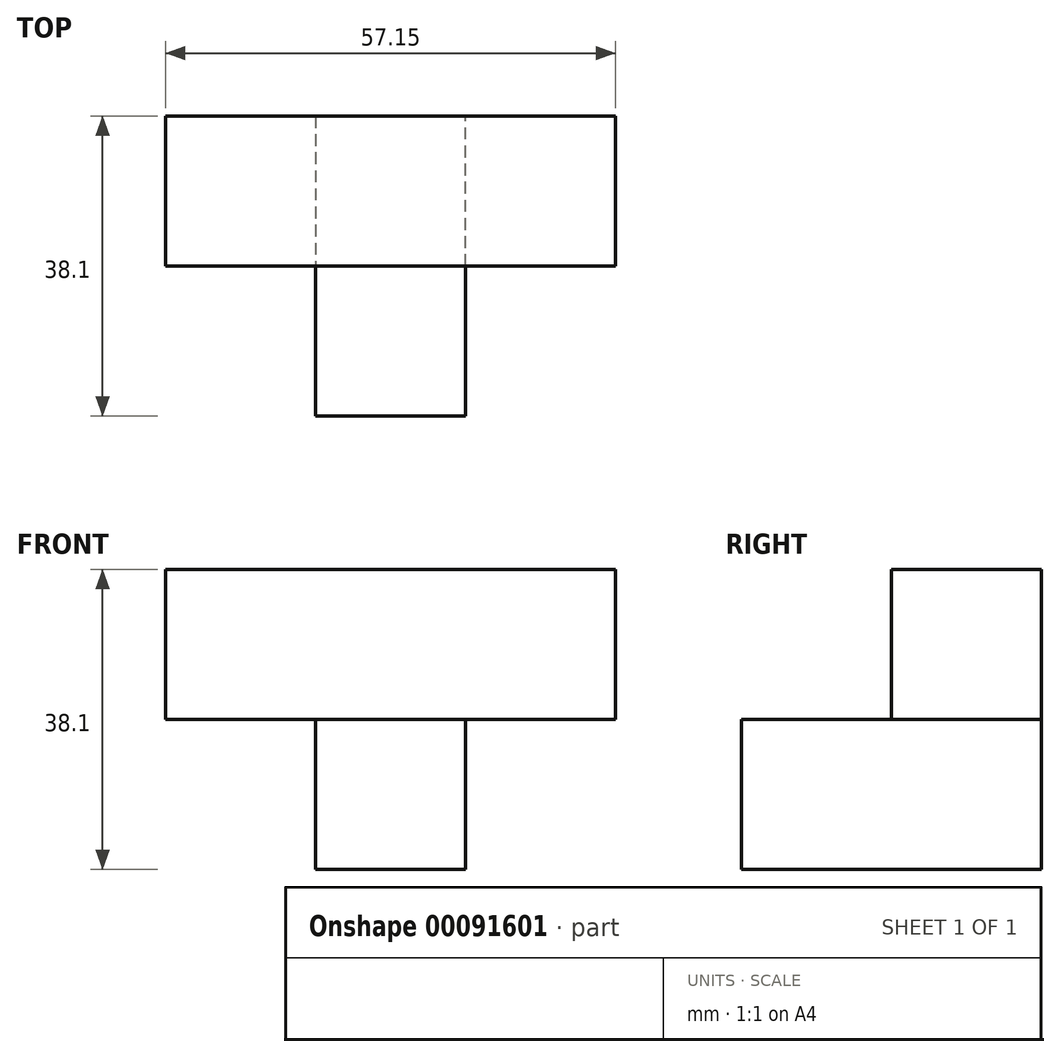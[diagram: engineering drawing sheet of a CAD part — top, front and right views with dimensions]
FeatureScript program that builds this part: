
annotation { "Feature Type Name" : "Feature", "Feature Type Description" : "" }
export const myFeature = defineFeature(function(context is Context, id is Id, definition is map)
    precondition{}
    {
        {
            var Q0;
            Q0=qCreatedBy(makeId("Top.planeOp"),FACE);
            var sketch = newSketch(context, id + "F0", { "sketchPlane" : qUnion([Q0])});
            skLineSegment(sketch, "E0.bottom", {"start": v(-19.05, 35.05) * mm, "end": v(0, 35.05) * mm});
            skLineSegment(sketch, "E0.top", {"start": v(-19.05, 16) * mm, "end": v(0, 16) * mm});
            skLineSegment(sketch, "E0.left", {"start": v(-19.05, 35.05) * mm, "end": v(-19.05, 16) * mm});
            skLineSegment(sketch, "E0.right", {"start": v(0, 35.05) * mm, "end": v(0, 16) * mm});
            skSolve(sketch);
        }
        {
            var Q0;
            Q0 = qSketchRegion(id + "F0", true);
            var Q1;
            Q1=makeQuery(id+"F0.imprint","IMPRINT",FACE,{"disambiguationData":[TD([[makeQuery(id+"F0.imprint","IMPRINT",EDGE,{"derivedFrom":sQuery(id+"F0.wireOp",EDGE,"E0.bottom")}),-1.0]])]});
            extrude(context, id + "F1", {"entities" : qUnion([Q0, Q1]), "depth" : 19.05 * mm});
        }
        {
            var Q0;
            Q0=makeQuery(id+"F1.opExtrude","CAP_FACE",FACE,{"disambiguationData":[OSD([sQuery(id+"F0.wireOp",EDGE,"E0.bottom"),sQuery(id+"F0.wireOp",EDGE,"E0.top"),sQuery(id+"F0.wireOp",EDGE,"E0.left"),sQuery(id+"F0.wireOp",EDGE,"E0.right")])],"isStart":false});
            extrude(context, id + "F2", {"entities" : qUnion([Q0]), "operationType" : NewBodyOperationType.ADD, "depth" : 19.05 * mm});
        }
        {
            var Q0;
            {var subQ0=sQuery(id+"F0.wireOp",EDGE,"E0.top");Q0=makeQuery(id+"F2.boolean.opBoolean","MERGE",FACE,{"derivedFrom":[makeQuery(id+"F1.opExtrude","SWEPT_FACE",FACE,{"disambiguationData":[OSD([subQ0])]}),makeQuery(id+"F2.opExtrude","SWEPT_FACE",FACE,{"disambiguationData":[OSD([subQ0])]})]});}
            var sketch = newSketch(context, id + "F3", { "sketchPlane" : qUnion([Q0])});
            skLineSegment(sketch, "E1.bottom", {"start": v(-19.05, 0) * mm, "end": v(0, 0) * mm});
            skLineSegment(sketch, "E1.top", {"start": v(-19.05, 19.05) * mm, "end": v(0, 19.05) * mm});
            skLineSegment(sketch, "E1.left", {"start": v(-19.05, 0) * mm, "end": v(-19.05, 19.05) * mm});
            skLineSegment(sketch, "E1.right", {"start": v(0, 0) * mm, "end": v(0, 19.05) * mm});
            skSolve(sketch);
        }
        {
            var Q0;
            Q0 = qSketchRegion(id + "F3", true);
            extrude(context, id + "F4", {"entities" : qUnion([Q0]), "operationType" : NewBodyOperationType.ADD, "depth" : 19.05 * mm});
        }
        {
            var Q0;
            {var subQ0=sQuery(id+"F0.wireOp",EDGE,"E0.right");Q0=makeQuery(id+"F4.boolean.opBoolean","MERGE",FACE,{"derivedFrom":[makeQuery(id+"F2.boolean.opBoolean","MERGE",FACE,{"derivedFrom":[makeQuery(id+"F1.opExtrude","SWEPT_FACE",FACE,{"disambiguationData":[OSD([subQ0])]}),makeQuery(id+"F2.opExtrude","SWEPT_FACE",FACE,{"disambiguationData":[OSD([subQ0])]})]}),makeQuery(id+"F4.opExtrude","SWEPT_FACE",FACE,{"disambiguationData":[OSD([sQuery(id+"F3.wireOp",EDGE,"E1.right")])]})]});}
            var sketch = newSketch(context, id + "F5", { "sketchPlane" : qUnion([Q0])});
            skLineSegment(sketch, "E2.bottom", {"start": v(16, 38.1) * mm, "end": v(35.05, 38.1) * mm});
            skLineSegment(sketch, "E2.top", {"start": v(16, 19.05) * mm, "end": v(35.05, 19.05) * mm});
            skLineSegment(sketch, "E2.left", {"start": v(16, 38.1) * mm, "end": v(16, 19.05) * mm});
            skLineSegment(sketch, "E2.right", {"start": v(35.05, 38.1) * mm, "end": v(35.05, 19.05) * mm});
            skSolve(sketch);
        }
        {
            var Q0;
            Q0 = qSketchRegion(id + "F5", true);
            var Q1;
            Q1=makeQuery(id+"F5.imprint","IMPRINT",FACE,{"disambiguationData":[TD([[makeQuery(id+"F5.imprint","IMPRINT",EDGE,{"derivedFrom":sQuery(id+"F5.wireOp",EDGE,"E2.bottom")}),1.0]])]});
            extrude(context, id + "F6", {"entities" : qUnion([Q0, Q1]), "operationType" : NewBodyOperationType.ADD, "depth" : 19.05 * mm});
        }
        {
            var Q0;
            {var subQ0=sQuery(id+"F0.wireOp",EDGE,"E0.left");Q0=makeQuery(id+"F4.boolean.opBoolean","MERGE",FACE,{"derivedFrom":[makeQuery(id+"F2.boolean.opBoolean","MERGE",FACE,{"derivedFrom":[makeQuery(id+"F1.opExtrude","SWEPT_FACE",FACE,{"disambiguationData":[OSD([subQ0])]}),makeQuery(id+"F2.opExtrude","SWEPT_FACE",FACE,{"disambiguationData":[OSD([subQ0])]})]}),makeQuery(id+"F4.opExtrude","SWEPT_FACE",FACE,{"disambiguationData":[OSD([sQuery(id+"F3.wireOp",EDGE,"E1.left")])]})]});}
            var sketch = newSketch(context, id + "F7", { "sketchPlane" : qUnion([Q0])});
            skLineSegment(sketch, "E3.bottom", {"start": v(-35.05, 38.1) * mm, "end": v(-16, 38.1) * mm});
            skLineSegment(sketch, "E3.top", {"start": v(-35.05, 19.05) * mm, "end": v(-16, 19.05) * mm});
            skLineSegment(sketch, "E3.left", {"start": v(-35.05, 38.1) * mm, "end": v(-35.05, 19.05) * mm});
            skLineSegment(sketch, "E3.right", {"start": v(-16, 38.1) * mm, "end": v(-16, 19.05) * mm});
            skSolve(sketch);
        }
        {
            var Q0;
            Q0=makeQuery(id+"F7.imprint","IMPRINT",FACE,{"disambiguationData":[TD([[makeQuery(id+"F7.imprint","IMPRINT",EDGE,{"derivedFrom":sQuery(id+"F7.wireOp",EDGE,"E3.bottom")}),-1.0]])]});
            extrude(context, id + "F8", {"entities" : qUnion([Q0]), "operationType" : NewBodyOperationType.ADD, "depth" : 19.05 * mm});
        }
    });
